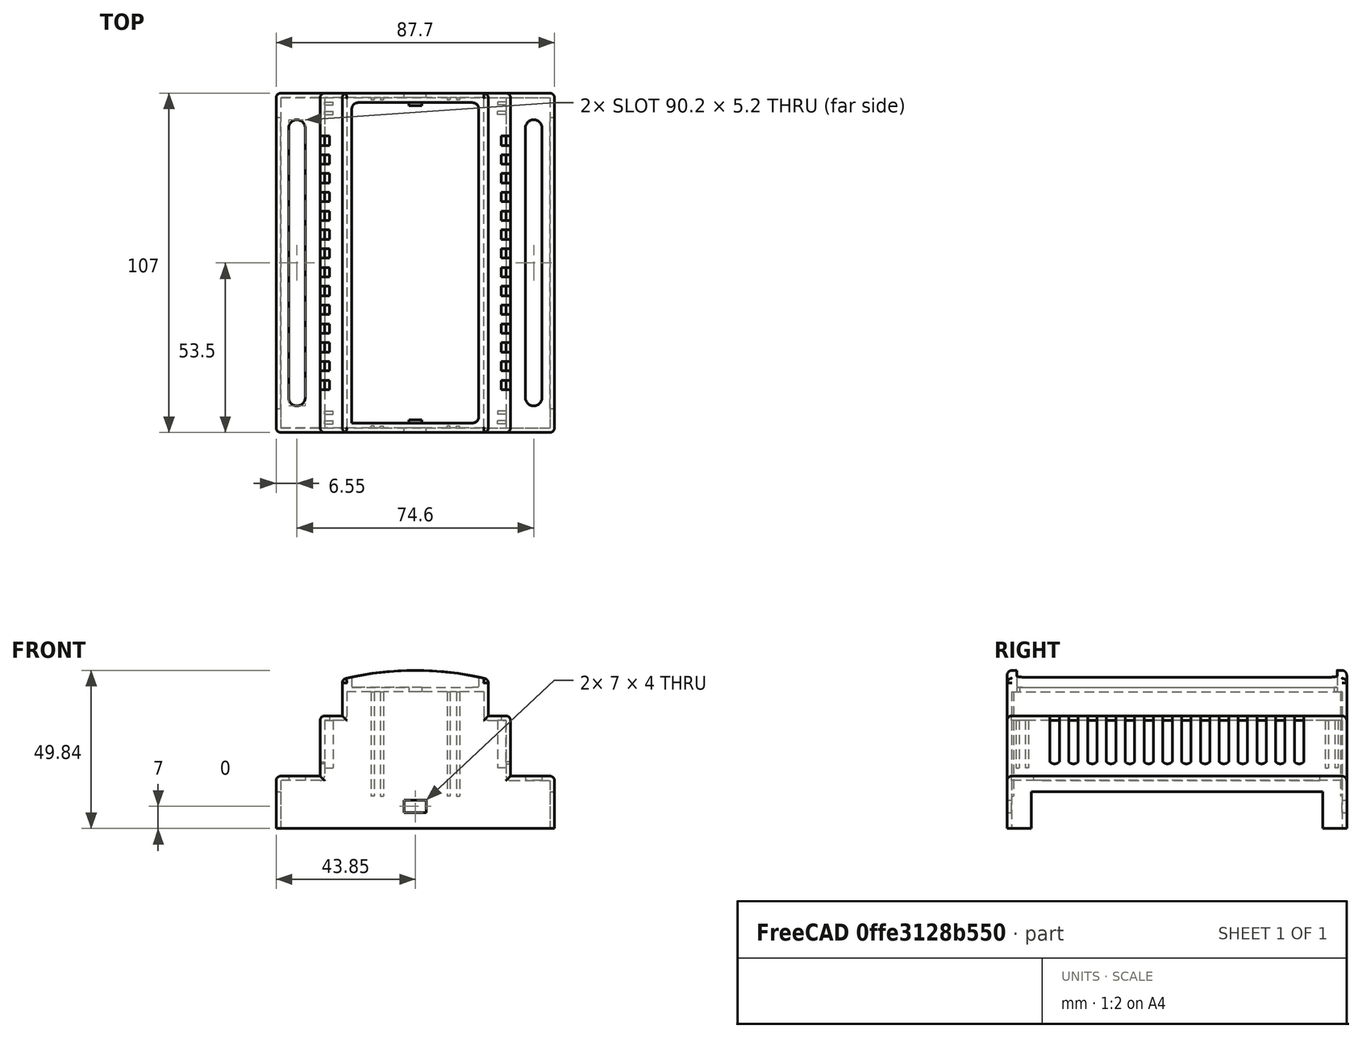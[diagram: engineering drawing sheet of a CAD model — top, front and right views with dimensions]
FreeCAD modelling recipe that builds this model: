
FCSTD DOCUMENT  (FreeCAD 1.0R39109 (Git))
Label: Parte de Arriba Vlad
License: All rights reserved
LicenseURL: https://en.wikipedia.org/wiki/All_rights_reserved
objects: Sketcher::SketchObject×15, PartDesign::Pad×9, PartDesign::Mirrored×7, PartDesign::Pocket×6, PartDesign::Fillet×4, PartDesign::Thickness×2, PartDesign::Plane×1, PartDesign::Body×1
note: 109 computed .brp shape members not serialized (recipe doc carries the construction recipe); baked Part::Feature solids carry a one-line shape summary decoded from their .brp

FEATURE [Sketcher::SketchObject] Sketch
  ArcFitTolerance = 1e-06
  AttachmentSupport = -> [XZ_Plane001]
  FullyConstrained = true
  MakeInternals = false
  MapMode = 5
  Placement = pos=(0,0,0) rot=(1,0,0;1.5708rad)
  sketch-geometry (12):
    g0: LineSegment StartX=-43.85 StartY=0 StartZ=0 EndX=43.85 EndY=0 EndZ=0
    g1: LineSegment StartX=-43.85 StartY=0 StartZ=0 EndX=-43.85 EndY=16.54 EndZ=0
    g2: LineSegment StartX=43.85 StartY=0 StartZ=0 EndX=43.85 EndY=16.54 EndZ=0
    g3: LineSegment StartX=-43.85 StartY=16.54 StartZ=0 EndX=-30 EndY=16.54 EndZ=0
    g4: LineSegment StartX=43.85 StartY=16.54 StartZ=0 EndX=30 EndY=16.54 EndZ=0
    g5: LineSegment StartX=-30 StartY=16.54 StartZ=0 EndX=-30 EndY=35.54 EndZ=0
    g6: LineSegment StartX=30 StartY=16.54 StartZ=0 EndX=30 EndY=35.54 EndZ=0
    g7: LineSegment StartX=-30 StartY=35.54 StartZ=0 EndX=-23 EndY=35.54 EndZ=0
    g8: LineSegment StartX=30 StartY=35.54 StartZ=0 EndX=23 EndY=35.54 EndZ=0
    g9: LineSegment StartX=23 StartY=35.54 StartZ=0 EndX=23 EndY=44.54 EndZ=0
    g10: LineSegment StartX=-23 StartY=35.54 StartZ=0 EndX=-23 EndY=44.54 EndZ=0
    g11: LineSegment StartX=-23 StartY=44.54 StartZ=0 EndX=23 EndY=44.54 EndZ=0
  constraints (36):
    c: Distance(g0) = 87.7
    c: PointOnObject(g0,g-1)
    c: PointOnObject(g0,g-1)
    c: Vertical(g1)
    c: Coincident(g1,g0)
    c: Vertical(g2)
    c: Coincident(g2,g0)
    c: Distance(g3) = 13.85
    c: Horizontal(g3)
    c: Coincident(g3,g1)
    c: Distance(g4) = 13.85
    c: Horizontal(g4)
    c: Coincident(g4,g2)
    c: Vertical(g5)
    c: Coincident(g5,g3)
    c: Vertical(g6)
    c: Coincident(g6,g4)
    c: Distance(g7) = 7
    c: Horizontal(g7)
    c: Coincident(g7,g5)
    c: Distance(g8) = 7
    c: Horizontal(g8)
    c: Coincident(g8,g6)
    c: Vertical(g9)
    c: Coincident(g9,g8)
    c: Vertical(g10)
    c: Coincident(g10,g7)
    c: Coincident(g11,g10)
    c: Coincident(g11,g9)
    c: Equal(g1,g2)
    c: Equal(g5,g6)
    c: Equal(g10,g9)
    c: Distance(g0,g11) = 44.54
    c: DistanceY(g1,g1) = 16.54
    c: Distance(g5,g0) = 35.54
    c: Distance(g10,g-2) = 23
FEATURE [PartDesign::Pad] Pad
  Direction = (0,-1,2e-16)
  Length = 107
  Length2 = 10
  Placement = pos=(0,0,0) rot=(1,0,0;1.5708rad)
  Profile = -> Sketch
  ReferenceAxis = -> Sketch [N_Axis]
  Refine = true
  Suppressed = false
  Type = 0
FEATURE [PartDesign::Thickness] Thickness
  Base = -> Pad
  BaseFeature = -> Pad
  Intersection = false
  Join = 0
  Mode = 0
  Placement = pos=(0,0,0) rot=(1,0,0;1.5708rad)
  Refine = true
  Reversed = true
  SupportTransform = false
  Suppressed = false
  Value = 1.4
FEATURE [PartDesign::Thickness] Thickness001
  Base = -> Thickness [Face1]
  BaseFeature = -> Thickness
  Intersection = false
  Join = 0
  Mode = 0
  Refine = true
  Reversed = true
  SupportTransform = false
  Suppressed = false
  Value = 1.4
FEATURE [Sketcher::SketchObject] Sketch001
  ArcFitTolerance = 1e-06
  AttachmentSupport = -> [Thickness001]
  FullyConstrained = true
  MakeInternals = false
  MapMode = 5
  Placement = pos=(-43.85,0,0) rot=(0.57735,-0.57735,-0.57735;2.0944rad)
  sketch-geometry (4):
    g0: LineSegment StartX=7.575 StartY=0 StartZ=0 EndX=99.425 EndY=0 EndZ=0
    g1: LineSegment StartX=99.425 StartY=0 StartZ=0 EndX=99.425 EndY=11.6 EndZ=0
    g2: LineSegment StartX=99.425 StartY=11.6 StartZ=0 EndX=7.575 EndY=11.6 EndZ=0
    g3: LineSegment StartX=7.575 StartY=11.6 StartZ=0 EndX=7.575 EndY=0 EndZ=0
  constraints (12):
    c: Coincident(g0,g1)
    c: Coincident(g1,g2)
    c: Coincident(g2,g3)
    c: Coincident(g3,g0)
    c: Horizontal(g0)
    c: Horizontal(g2)
    c: Vertical(g1)
    c: Vertical(g3)
    c: PointOnObject(g0,g-1)
    c: DistanceX(g2,g2) = 91.85
    c: DistanceY(g1,g1) = 11.6
    c: DistanceX(g-1,g0) = 7.575
FEATURE [PartDesign::Pocket] Pocket
  BaseFeature = -> Thickness001
  Direction = (1,0,0)
  Length = 5
  Length2 = 5
  Profile = -> Sketch001
  ReferenceAxis = -> Sketch001 [N_Axis]
  Refine = true
  Suppressed = false
  Type = 1
FEATURE [Sketcher::SketchObject] Sketch002
  ArcFitTolerance = 1e-06
  AttachmentSupport = -> [Pocket]
  FullyConstrained = true
  MakeInternals = false
  MapMode = 5
  Placement = pos=(0,4.2e-15,0) rot=(0,0.707107,0.707107;3.14159rad)
  sketch-geometry (4):
    g0: LineSegment StartX=-23 StartY=44.54 StartZ=0 EndX=23 EndY=44.54 EndZ=0
    g1: LineSegment StartX=-23 StartY=44.54 StartZ=0 EndX=-23 EndY=47.04 EndZ=0
    g2: LineSegment StartX=23 StartY=44.54 StartZ=0 EndX=23 EndY=47.04 EndZ=0
    g3: ArcOfCircle CenterX=1.7e-15 CenterY=-46.0243 CenterZ=0 NormalX=0 NormalY=0 NormalZ=1 AngleXU=0 Radius=95.8643 StartAngle=1.32851 EndAngle=1.81308
  constraints (13):
    c: Distance(g0) = 46
    c: Horizontal(g0)
    c: Distance(g-1,g0) = 44.54
    c: Distance(g0,g-2) = 23
    c: Distance(g1) = 2.5
    c: Coincident(g1,g0)
    c: Vertical(g1)
    c: Distance(g2) = 2.5
    c: Coincident(g2,g0)
    c: Vertical(g2)
    c: Coincident(g3,g1)
    c: Coincident(g3,g2)
    c: Distance(g3,g0) = -5.3
FEATURE [PartDesign::Pad] Pad001
  BaseFeature = -> Pocket
  Direction = (0,1,-2e-16)
  Length = 107
  Length2 = 10
  Profile = -> Sketch002
  ReferenceAxis = -> Sketch002 [N_Axis]
  Refine = true
  Suppressed = false
  Type = 0
FEATURE [Sketcher::SketchObject] Sketch003
  ArcFitTolerance = 1e-06
  AttachmentSupport = -> [Pad001]
  ExternalGeometry = -> [Pad001]
  FullyConstrained = true
  MakeInternals = false
  MapMode = 5
  Placement = pos=(0,4.2e-15,0) rot=(0,0.707107,0.707107;3.14159rad)
  sketch-geometry (4):
    g0: LineSegment StartX=-23 StartY=44.54 StartZ=0 EndX=-23 EndY=47.04 EndZ=0
    g1: LineSegment StartX=23 StartY=44.54 StartZ=0 EndX=23 EndY=47.04 EndZ=0
    g2: ArcOfCircle CenterX=4.82e-14 CenterY=-46.0243 CenterZ=0 NormalX=0 NormalY=0 NormalZ=1 AngleXU=0 Radius=95.8643 StartAngle=1.32851 EndAngle=1.81308
    g3: LineSegment StartX=-23 StartY=44.54 StartZ=0 EndX=23 EndY=44.54 EndZ=0
  constraints (9):
    c: Distance(g0) = 2.5
    c: Coincident(g2,g0)
    c: Coincident(g2,g1)
    c: Coincident(g3,g-3)
    c: Coincident(g3,g-3)
    c: Perpendicular(g0,g3) = 4.71239
    c: Distance(g2,g3) = -5.3
    c: Perpendicular(g1,g3) = 4.71239
    c: DistanceY(g1,g1) = 2.5
FEATURE [PartDesign::Pad] Pad002
  BaseFeature = -> Pad001
  Direction = (0,1,-2e-16)
  Length = 3
  Length2 = 10
  Profile = -> Sketch003
  ReferenceAxis = -> Sketch003 [N_Axis]
  Refine = true
  Reversed = true
  Suppressed = false
  Type = 0
FEATURE [Sketcher::SketchObject] Sketch004
  ArcFitTolerance = 1e-06
  AttachmentSupport = -> [Pad002]
  ExternalGeometry = -> [Pad002]
  FullyConstrained = true
  MakeInternals = false
  MapMode = 5
  Placement = pos=(0,-107,0) rot=(1,0,0;1.5708rad)
  sketch-geometry (4):
    g0: LineSegment StartX=-23 StartY=44.54 StartZ=0 EndX=23 EndY=44.54 EndZ=0
    g1: LineSegment StartX=23 StartY=44.54 StartZ=0 EndX=23 EndY=47.04 EndZ=0
    g2: LineSegment StartX=-23 StartY=44.54 StartZ=0 EndX=-23 EndY=47.04 EndZ=0
    g3: ArcOfCircle CenterX=3.7756e-12 CenterY=-46.0243 CenterZ=0 NormalX=0 NormalY=0 NormalZ=1 AngleXU=0 Radius=95.8643 StartAngle=1.32851 EndAngle=1.81308
  constraints (9):
    c: Coincident(g0,g-5)
    c: Coincident(g0,g-6)
    c: Coincident(g1,g0)
    c: Coincident(g1,g-6)
    c: Coincident(g2,g0)
    c: Coincident(g2,g-5)
    c: Coincident(g3,g2)
    c: Coincident(g3,g1)
    c: Tangent(g3,g-4)
FEATURE [PartDesign::Pad] Pad003
  BaseFeature = -> Pad002
  Direction = (0,-1,2e-16)
  Length = 3
  Length2 = 10
  Profile = -> Sketch004
  ReferenceAxis = -> Sketch004 [N_Axis]
  Refine = true
  Reversed = true
  Suppressed = false
  Type = 0
FEATURE [Sketcher::SketchObject] Sketch005
  ArcFitTolerance = 1e-06
  AttachmentSupport = -> [Pad003]
  ExternalGeometry = -> [Pad003]
  FullyConstrained = true
  MakeInternals = false
  MapMode = 5
  Placement = pos=(23,-8.5e-15,1.304e-13) rot=(0.57735,0.57735,0.57735;2.0944rad)
  sketch-geometry (4):
    g0: LineSegment StartX=-104 StartY=49.84 StartZ=0 EndX=-104 EndY=44.54 EndZ=0
    g1: LineSegment StartX=-104 StartY=44.54 StartZ=0 EndX=-3 EndY=44.54 EndZ=0
    g2: LineSegment StartX=-3 StartY=49.84 StartZ=0 EndX=-3 EndY=44.54 EndZ=0
    g3: LineSegment StartX=-104 StartY=49.84 StartZ=0 EndX=-3 EndY=49.84 EndZ=0
  constraints (8):
    c: Coincident(g0,g-5)
    c: Coincident(g0,g-3)
    c: Coincident(g1,g0)
    c: Coincident(g1,g-3)
    c: Coincident(g2,g-4)
    c: Coincident(g2,g1)
    c: Coincident(g3,g0)
    c: Coincident(g3,g2)
FEATURE [PartDesign::Pad] Pad004
  BaseFeature = -> Pad003
  Direction = (1,0,5.8e-15)
  Length = 3
  Length2 = 10
  Profile = -> Sketch005
  ReferenceAxis = -> Sketch005 [N_Axis]
  Refine = true
  Reversed = true
  Suppressed = false
  Type = 0
FEATURE [PartDesign::Mirrored] Mirrored
  BaseFeature = -> Pad004
  MirrorPlane = -> YZ_Plane001
  Originals = -> [Pad004]
  Refine = true
  Suppressed = false
  TransformMode = 0
FEATURE [Sketcher::SketchObject] Sketch006
  ArcFitTolerance = 1e-06
  AttachmentSupport = -> [Mirrored]
  FullyConstrained = true
  MakeInternals = false
  MapMode = 5
  Placement = pos=(0,7.3e-15,16.54) rot=(0,0,1;0rad)
  sketch-geometry (4):
    g0: ArcOfCircle CenterX=37.3 CenterY=-11 CenterZ=0 NormalX=0 NormalY=0 NormalZ=1 AngleXU=0 Radius=2.6 StartAngle=2.2037e-12 EndAngle=3.14159
    g1: ArcOfCircle CenterX=37.3 CenterY=-96 CenterZ=0 NormalX=0 NormalY=0 NormalZ=1 AngleXU=0 Radius=2.6 StartAngle=3.14159 EndAngle=6.28319
    g2: LineSegment StartX=39.9 StartY=-11 StartZ=0 EndX=39.9 EndY=-96 EndZ=0
    g3: LineSegment StartX=34.7 StartY=-11 StartZ=0 EndX=34.7 EndY=-96 EndZ=0
  constraints (10):
    c: Tangent(g0,g2) = 1.5708
    c: Tangent(g0,g3) = -1.5708
    c: Tangent(g1,g2) = 1.5708
    c: Tangent(g1,g3) = -1.5708
    c: Equal(g0,g1)
    c: Vertical(g2)
    c: Distance(g2,g3) = 5.2
    c: DistanceY(g2,g2) = 85
    c: Distance(g0,g-2) = 37.3
    c: Distance(g0,g-1) = 11
FEATURE [PartDesign::Pocket] Pocket001
  BaseFeature = -> Mirrored
  Direction = (0,0,-1)
  Length = 5
  Length2 = 5
  Profile = -> Sketch006
  ReferenceAxis = -> Sketch006 [N_Axis]
  Refine = true
  Suppressed = false
  Type = 0
FEATURE [PartDesign::Mirrored] Mirrored001
  BaseFeature = -> Pocket001
  MirrorPlane = -> YZ_Plane001
  Originals = -> [Pocket001]
  Refine = true
  Suppressed = false
  TransformMode = 0
FEATURE [Sketcher::SketchObject] Sketch007
  ArcFitTolerance = 1e-06
  AttachmentSupport = -> [Mirrored001]
  ExternalGeometry = -> [Mirrored001]
  FullyConstrained = true
  MakeInternals = false
  MapMode = 5
  Placement = pos=(30,0,0) rot=(0.57735,0.57735,0.57735;2.0944rad)
  sketch-geometry (57):
    g0: LineSegment [constr] StartX=-53.5 StartY=35.54 StartZ=0 EndX=-53.5 EndY=16.54 EndZ=0
    g1: LineSegment StartX=-16.4625 StartY=35.54 StartZ=0 EndX=-13.4995 EndY=35.54 EndZ=0
    g2: LineSegment StartX=-13.4995 StartY=35.54 StartZ=0 EndX=-13.4995 EndY=21.04 EndZ=0
    g3: LineSegment StartX=-16.4625 StartY=35.54 StartZ=0 EndX=-16.4625 EndY=21.04 EndZ=0
    g4: ArcOfCircle CenterX=-14.981 CenterY=22.3836 CenterZ=0 NormalX=0 NormalY=0 NormalZ=1 AngleXU=0 Radius=2 StartAngle=3.8782 EndAngle=5.54658
    g5: LineSegment StartX=-22.3885 StartY=35.54 StartZ=0 EndX=-19.4255 EndY=35.54 EndZ=0
    g6: LineSegment StartX=-19.4255 StartY=35.54 StartZ=0 EndX=-19.4255 EndY=21.04 EndZ=0
    g7: LineSegment StartX=-22.3885 StartY=35.54 StartZ=0 EndX=-22.3885 EndY=21.04 EndZ=0
    g8: ArcOfCircle CenterX=-20.907 CenterY=22.3836 CenterZ=0 NormalX=0 NormalY=0 NormalZ=1 AngleXU=0 Radius=2 StartAngle=3.8782 EndAngle=5.54658
    g9: LineSegment StartX=-28.3145 StartY=35.54 StartZ=0 EndX=-25.3515 EndY=35.54 EndZ=0
    g10: LineSegment StartX=-25.3515 StartY=35.54 StartZ=0 EndX=-25.3515 EndY=21.04 EndZ=0
    g11: LineSegment StartX=-28.3145 StartY=35.54 StartZ=0 EndX=-28.3145 EndY=21.04 EndZ=0
    g12: ArcOfCircle CenterX=-26.833 CenterY=22.3836 CenterZ=0 NormalX=0 NormalY=0 NormalZ=1 AngleXU=0 Radius=2 StartAngle=3.8782 EndAngle=5.54658
    g13: LineSegment StartX=-34.2405 StartY=35.54 StartZ=0 EndX=-31.2775 EndY=35.54 EndZ=0
    g14: LineSegment StartX=-34.2405 StartY=35.54 StartZ=0 EndX=-34.2405 EndY=21.04 EndZ=0
    g15: LineSegment StartX=-31.2775 StartY=35.54 StartZ=0 EndX=-31.2775 EndY=21.04 EndZ=0
    g16: ArcOfCircle CenterX=-32.759 CenterY=22.3836 CenterZ=0 NormalX=0 NormalY=0 NormalZ=1 AngleXU=0 Radius=2 StartAngle=3.8782 EndAngle=5.54658
    g17: LineSegment StartX=-40.1665 StartY=35.54 StartZ=0 EndX=-37.2035 EndY=35.54 EndZ=0
    g18: LineSegment StartX=-37.2035 StartY=35.54 StartZ=0 EndX=-37.2035 EndY=21.04 EndZ=0
    g19: LineSegment StartX=-40.1665 StartY=35.54 StartZ=0 EndX=-40.1665 EndY=21.04 EndZ=0
    g20: ArcOfCircle CenterX=-38.685 CenterY=22.3836 CenterZ=0 NormalX=0 NormalY=0 NormalZ=1 AngleXU=0 Radius=2 StartAngle=3.8782 EndAngle=5.54658
    g21: LineSegment StartX=-46.0925 StartY=35.54 StartZ=0 EndX=-43.1295 EndY=35.54 EndZ=0
    g22: LineSegment StartX=-43.1295 StartY=35.54 StartZ=0 EndX=-43.1295 EndY=21.04 EndZ=0
    g23: LineSegment StartX=-46.0925 StartY=35.54 StartZ=0 EndX=-46.0925 EndY=21.04 EndZ=0
    g24: ArcOfCircle CenterX=-44.611 CenterY=22.3836 CenterZ=0 NormalX=0 NormalY=0 NormalZ=1 AngleXU=0 Radius=2 StartAngle=3.8782 EndAngle=5.54658
    g25: LineSegment StartX=-52.0185 StartY=35.54 StartZ=0 EndX=-49.0555 EndY=35.54 EndZ=0
    g26: LineSegment StartX=-49.0555 StartY=35.54 StartZ=0 EndX=-49.0555 EndY=21.04 EndZ=0
    g27: LineSegment StartX=-52.0185 StartY=35.54 StartZ=0 EndX=-52.0185 EndY=21.04 EndZ=0
    g28: ArcOfCircle CenterX=-50.537 CenterY=22.3836 CenterZ=0 NormalX=0 NormalY=0 NormalZ=1 AngleXU=0 Radius=2 StartAngle=3.8782 EndAngle=5.54658
    g29: LineSegment StartX=-57.9445 StartY=35.54 StartZ=0 EndX=-54.9815 EndY=35.54 EndZ=0
    g30: LineSegment StartX=-54.9815 StartY=35.54 StartZ=0 EndX=-54.9815 EndY=21.04 EndZ=0
    g31: LineSegment StartX=-57.9445 StartY=35.54 StartZ=0 EndX=-57.9445 EndY=21.04 EndZ=0
    g32: ArcOfCircle CenterX=-56.463 CenterY=22.3836 CenterZ=0 NormalX=0 NormalY=0 NormalZ=1 AngleXU=0 Radius=2 StartAngle=3.8782 EndAngle=5.54658
    g33: LineSegment StartX=-63.8705 StartY=35.54 StartZ=0 EndX=-60.9075 EndY=35.54 EndZ=0
    g34: LineSegment StartX=-60.9075 StartY=35.54 StartZ=0 EndX=-60.9075 EndY=21.04 EndZ=0
    g35: LineSegment StartX=-63.8705 StartY=35.54 StartZ=0 EndX=-63.8705 EndY=21.04 EndZ=0
    g36: ArcOfCircle CenterX=-62.389 CenterY=22.3836 CenterZ=0 NormalX=0 NormalY=0 NormalZ=1 AngleXU=0 Radius=2 StartAngle=3.8782 EndAngle=5.54658
    g37: LineSegment StartX=-69.7965 StartY=35.54 StartZ=0 EndX=-66.8335 EndY=35.54 EndZ=0
    g38: LineSegment StartX=-66.8335 StartY=35.54 StartZ=0 EndX=-66.8335 EndY=21.04 EndZ=0
    g39: LineSegment StartX=-69.7965 StartY=35.54 StartZ=0 EndX=-69.7965 EndY=21.04 EndZ=0
    g40: ArcOfCircle CenterX=-68.315 CenterY=22.3836 CenterZ=0 NormalX=0 NormalY=0 NormalZ=1 AngleXU=0 Radius=2 StartAngle=3.8782 EndAngle=5.54658
    g41: LineSegment StartX=-75.7225 StartY=35.54 StartZ=0 EndX=-72.7595 EndY=35.54 EndZ=0
    g42: LineSegment StartX=-72.7595 StartY=35.54 StartZ=0 EndX=-72.7595 EndY=21.04 EndZ=0
    g43: LineSegment StartX=-75.7225 StartY=35.54 StartZ=0 EndX=-75.7225 EndY=21.04 EndZ=0
    g44: ArcOfCircle CenterX=-74.241 CenterY=22.3836 CenterZ=0 NormalX=0 NormalY=0 NormalZ=1 AngleXU=0 Radius=2 StartAngle=3.8782 EndAngle=5.54658
    g45: LineSegment StartX=-81.6485 StartY=35.54 StartZ=0 EndX=-78.6855 EndY=35.54 EndZ=0
    g46: LineSegment StartX=-78.6855 StartY=35.54 StartZ=0 EndX=-78.6855 EndY=21.04 EndZ=0
    g47: LineSegment StartX=-81.6485 StartY=35.54 StartZ=0 EndX=-81.6485 EndY=21.04 EndZ=0
    g48: ArcOfCircle CenterX=-80.167 CenterY=22.3836 CenterZ=0 NormalX=0 NormalY=0 NormalZ=1 AngleXU=0 Radius=2 StartAngle=3.8782 EndAngle=5.54658
    g49: LineSegment StartX=-87.5745 StartY=35.54 StartZ=0 EndX=-84.6115 EndY=35.54 EndZ=0
    g50: LineSegment StartX=-84.6115 StartY=35.54 StartZ=0 EndX=-84.6115 EndY=21.04 EndZ=0
    g51: LineSegment StartX=-87.5745 StartY=35.54 StartZ=0 EndX=-87.5745 EndY=21.04 EndZ=0
    g52: ArcOfCircle CenterX=-86.093 CenterY=22.3836 CenterZ=0 NormalX=0 NormalY=0 NormalZ=1 AngleXU=0 Radius=2 StartAngle=3.8782 EndAngle=5.54658
    g53: LineSegment StartX=-93.5005 StartY=35.54 StartZ=0 EndX=-90.5375 EndY=35.54 EndZ=0
    g54: LineSegment StartX=-90.5375 StartY=35.54 StartZ=0 EndX=-90.5375 EndY=21.04 EndZ=0
    g55: LineSegment StartX=-93.5005 StartY=35.54 StartZ=0 EndX=-93.5005 EndY=21.04 EndZ=0
    g56: ArcOfCircle CenterX=-92.019 CenterY=22.3836 CenterZ=0 NormalX=0 NormalY=0 NormalZ=1 AngleXU=0 Radius=2 StartAngle=3.8782 EndAngle=5.54658
  constraints (184):
    c: Symmetric(g-4,g-4,g0)
    c: Symmetric(g-3,g-3,g0)
    c: PointOnObject(g1,g-4)
    c: PointOnObject(g1,g-4)
    c: Distance(g2) = 14.5
    c: Vertical(g2)
    c: Coincident(g2,g1)
    c: Vertical(g3)
    c: Coincident(g3,g1)
    c: Coincident(g4,g3)
    c: Coincident(g4,g2)
    c: DistanceX(g1,g1) = 2.963
    c: Radius(g4) = 2
    c: Distance(g5) = 2.963
    c: Horizontal(g5)
    c: PointOnObject(g5,g-4)
    c: Vertical(g6)
    c: Coincident(g6,g5)
    c: Vertical(g7)
    c: Coincident(g7,g5)
    c: Equal(g2,g3)
    c: Equal(g3,g6)
    c: Equal(g6,g7)
    c: Distance(g3,g6) = 2.963
    c: Coincident(g8,g7)
    c: Coincident(g8,g6)
    c: Equal(g4,g8)
    c: Horizontal(g9)
    c: PointOnObject(g9,g-4)
    c: Vertical(g10)
    c: Coincident(g10,g9)
    c: Vertical(g11)
    c: Coincident(g11,g9)
    c: Coincident(g12,g11)
    c: Coincident(g12,g10)
    c: Equal(g5,g9)
    c: Equal(g6,g10)
    c: Equal(g10,g11)
    c: Equal(g4,g12)
    c: Distance(g7,g10) = 2.963
    c: PointOnObject(g13,g-4)
    c: PointOnObject(g13,g-4)
    c: Vertical(g14)
    c: Coincident(g14,g13)
    c: Vertical(g15)
    c: Coincident(g15,g13)
    c: Coincident(g16,g14)
    c: Coincident(g16,g15)
    c: Equal(g15,g14)
    c: Equal(g14,g2)
    c: Equal(g1,g13)
    c: Distance(g11,g15) = 2.963
    c: Equal(g4,g16)
    c: PointOnObject(g17,g-4)
    c: PointOnObject(g17,g-4)
    c: Vertical(g18)
    c: Coincident(g18,g17)
    c: Vertical(g19)
    c: Coincident(g19,g17)
    c: Coincident(g20,g19)
    c: Coincident(g20,g18)
    c: Distance(g14,g18) = 2.963
    c: Equal(g2,g18)
    c: Equal(g18,g19)
    c: Equal(g1,g17)
    c: Equal(g4,g20)
    c: PointOnObject(g21,g-4)
    c: PointOnObject(g21,g-4)
    c: Vertical(g22)
    c: Coincident(g22,g21)
    c: Vertical(g23)
    c: Coincident(g23,g21)
    c: Coincident(g24,g23)
    c: Coincident(g24,g22)
    c: Equal(g1,g21)
    c: Equal(g22,g23)
    c: Equal(g23,g2)
    c: Distance(g19,g22) = 2.963
    c: Equal(g4,g24)
    c: PointOnObject(g25,g-4)
    c: PointOnObject(g25,g-4)
    c: Vertical(g26)
    c: Coincident(g26,g25)
    c: Vertical(g27)
    c: Coincident(g27,g25)
    c: Coincident(g28,g27)
    c: Coincident(g28,g26)
    c: Equal(g2,g26)
    c: Equal(g26,g27)
    c: Equal(g1,g25)
    c: Equal(g4,g28)
    c: Distance(g23,g26) = 2.963
    c: PointOnObject(g29,g-4)
    c: PointOnObject(g29,g-4)
    c: Coincident(g30,g29)
    c: Vertical(g30)
    c: Coincident(g31,g29)
    c: Vertical(g31)
    c: Equal(g30,g31)
    c: Equal(g31,g3)
    c: Coincident(g32,g31)
    c: Coincident(g32,g30)
    c: Equal(g4,g32)
    c: Equal(g29,g1)
    c: Distance(g27,g30) = 2.963
    c: PointOnObject(g33,g-4)
    c: PointOnObject(g33,g-4)
    c: Coincident(g34,g33)
    c: Vertical(g34)
    c: Coincident(g35,g33)
    c: Vertical(g35)
    c: Equal(g35,g34)
    c: Equal(g34,g31)
    c: Equal(g33,g29)
    c: Coincident(g36,g35)
    c: Coincident(g36,g34)
    c: Equal(g32,g36)
    c: Distance(g31,g34) = 2.963
    c: PointOnObject(g37,g-4)
    c: PointOnObject(g37,g-4)
    c: Coincident(g38,g37)
    c: Vertical(g38)
    c: Coincident(g39,g37)
    c: Vertical(g39)
    c: Coincident(g40,g39)
    c: Coincident(g40,g38)
    c: Equal(g38,g39)
    c: Equal(g39,g35)
    c: Equal(g40,g36)
    c: Equal(g33,g37)
    c: Distance(g35,g38) = 2.963
    c: PointOnObject(g41,g-4)
    c: PointOnObject(g41,g-4)
    c: Coincident(g42,g41)
    c: Vertical(g42)
    c: Coincident(g43,g41)
    c: Vertical(g43)
    c: Coincident(g44,g43)
    c: Coincident(g44,g42)
    c: Equal(g43,g42)
    c: Equal(g42,g39)
    c: Equal(g41,g37)
    c: Equal(g44,g40)
    c: Distance(g39,g42) = 2.963
    c: PointOnObject(g45,g-4)
    c: PointOnObject(g45,g-4)
    c: Coincident(g46,g45)
    c: Vertical(g46)
    c: Coincident(g47,g45)
    c: Vertical(g47)
    c: Coincident(g48,g47)
    c: Coincident(g48,g46)
    c: Equal(g47,g46)
    c: Equal(g46,g43)
    c: Equal(g45,g41)
    c: Equal(g44,g48)
    c: Distance(g43,g46) = 2.963
    c: PointOnObject(g49,g-4)
    c: PointOnObject(g49,g-4)
    c: Coincident(g50,g49)
    c: Vertical(g50)
    c: Coincident(g51,g49)
    c: Vertical(g51)
    c: Coincident(g52,g51)
    c: Coincident(g52,g50)
    c: Equal(g51,g50)
    c: Equal(g50,g47)
    c: Equal(g49,g45)
    c: Equal(g48,g52)
    c: Distance(g47,g50) = 2.963
    c: PointOnObject(g53,g-4)
    c: PointOnObject(g53,g-4)
    c: Coincident(g54,g53)
    c: Vertical(g54)
    c: Coincident(g55,g53)
    c: Vertical(g55)
    c: Coincident(g56,g55)
    c: Coincident(g56,g54)
    c: Equal(g55,g54)
    c: Equal(g54,g51)
    c: Equal(g56,g52)
    c: Equal(g53,g49)
    c: Distance(g51,g54) = 2.963
    c: Distance(g0,g27) = 1.4815
FEATURE [PartDesign::Pocket] Pocket002
  BaseFeature = -> Mirrored001
  Direction = (-1,0,0)
  Length = 2.963
  Length2 = 5
  Profile = -> Sketch007
  ReferenceAxis = -> Sketch007 [N_Axis]
  Refine = true
  Suppressed = false
  Type = 0
FEATURE [PartDesign::Mirrored] Mirrored002
  BaseFeature = -> Pocket002
  MirrorPlane = -> YZ_Plane001
  Originals = -> [Pocket002]
  Refine = true
  Suppressed = false
  TransformMode = 0
FEATURE [PartDesign::Fillet] Fillet
  Base = -> Mirrored002 [Edge272,Edge110,Edge99,Edge166,Edge114,Edge118,Edge122,Edge126,Edge130,Edge134,Edge138,Edge142,Edge146,Edge150,Edge154,Edge158,Edge162,Edge20,Edge98,Edge97,Edge96]
  BaseFeature = -> Mirrored002
  Radius = 1.5
  Refine = true
  SupportTransform = false
  Suppressed = false
  UseAllEdges = false
FEATURE [PartDesign::Mirrored] Mirrored003
  BaseFeature = -> Fillet
  MirrorPlane = -> YZ_Plane001
  Originals = -> [Fillet]
  Refine = true
  Suppressed = false
  TransformMode = 0
FEATURE [Sketcher::SketchObject] Sketch008
  ArcFitTolerance = 1e-06
  AttachmentSupport = -> [Mirrored003]
  FullyConstrained = true
  MakeInternals = false
  MapMode = 5
  Placement = pos=(0,-107,3.53e-14) rot=(1,0,0;1.5708rad)
  sketch-geometry (4):
    g0: LineSegment StartX=-3.5 StartY=9 StartZ=0 EndX=3.5 EndY=9 EndZ=0
    g1: LineSegment StartX=-3.5 StartY=9 StartZ=0 EndX=-3.5 EndY=5 EndZ=0
    g2: LineSegment StartX=3.5 StartY=9 StartZ=0 EndX=3.5 EndY=5 EndZ=0
    g3: LineSegment StartX=-3.5 StartY=5 StartZ=0 EndX=3.5 EndY=5 EndZ=0
  constraints (12):
    c: Distance(g0) = 7
    c: Horizontal(g0)
    c: Vertical(g1)
    c: Coincident(g1,g0)
    c: Distance(g2) = 4
    c: Vertical(g2)
    c: Coincident(g2,g0)
    c: Coincident(g3,g1)
    c: Coincident(g3,g2)
    c: Distance(g-2,g1) = 3.5
    c: Equal(g2,g1)
    c: Distance(g-1,g3) = 5
FEATURE [PartDesign::Pocket] Pocket003
  BaseFeature = -> Mirrored003
  Direction = (0,1,-2e-16)
  Length = 5
  Length2 = 5
  Profile = -> Sketch008
  ReferenceAxis = -> Sketch008 [N_Axis]
  Refine = true
  Suppressed = false
  Type = 1
FEATURE [Sketcher::SketchObject] Sketch009
  ArcFitTolerance = 1e-06
  AttachmentSupport = -> [Pocket003]
  ExternalGeometry = -> [Pocket003]
  FullyConstrained = true
  MakeInternals = false
  MapMode = 5
  Placement = pos=(0,-104,0) rot=(1,0,0;1.5708rad)
  sketch-geometry (8):
    g0: LineSegment StartX=-23 StartY=47.04 StartZ=0 EndX=-23 EndY=49.84 EndZ=0
    g1: LineSegment StartX=-23 StartY=49.84 StartZ=0 EndX=-20 EndY=49.84 EndZ=0
    g2: LineSegment StartX=-20 StartY=49.84 StartZ=0 EndX=-20 EndY=47.7305 EndZ=0
    g3: ArcOfCircle CenterX=9.71783e-05 CenterY=-46.0247 CenterZ=0 NormalX=0 NormalY=0 NormalZ=1 AngleXU=0 Radius=95.8647 StartAngle=1.78097 EndAngle=1.81308
    g4: LineSegment StartX=20 StartY=49.84 StartZ=0 EndX=23 EndY=49.84 EndZ=0
    g5: LineSegment StartX=23 StartY=49.84 StartZ=0 EndX=23 EndY=47.04 EndZ=0
    g6: LineSegment StartX=20 StartY=49.84 StartZ=0 EndX=20 EndY=47.7305 EndZ=0
    g7: ArcOfCircle CenterX=-7.58465e-05 CenterY=-46.0246 CenterZ=0 NormalX=0 NormalY=0 NormalZ=1 AngleXU=0 Radius=95.8646 StartAngle=1.32851 EndAngle=1.36062
  constraints (19):
    c: Coincident(g0,g-6)
    c: Coincident(g0,g-6)
    c: Coincident(g1,g0)
    c: Coincident(g1,g-5)
    c: Coincident(g2,g1)
    c: Coincident(g2,g-4)
    c: Coincident(g3,g0)
    c: Coincident(g3,g2)
    c: Tangent(g3,g-3)
    c: Coincident(g4,g-8)
    c: Coincident(g4,g-9)
    c: Coincident(g5,g4)
    c: PointOnObject(g5,g-10)
    c: Vertical(g5)
    c: Coincident(g6,g4)
    c: Coincident(g6,g-10)
    c: Coincident(g7,g6)
    c: Coincident(g7,g5)
    c: Tangent(g7,g-10)
FEATURE [PartDesign::Pocket] Pocket004
  BaseFeature = -> Pocket003
  Direction = (0,1,-2e-16)
  Length = 0
  Length2 = 5
  Profile = -> Sketch009
  ReferenceAxis = -> Sketch009 [N_Axis]
  Refine = true
  Suppressed = false
  Type = 3
  UpToFace = -> Pocket003 [Face89]
FEATURE [PartDesign::Mirrored] Mirrored004
  BaseFeature = -> Pocket004
  MirrorPlane = -> YZ_Plane001
  Originals = -> [Fillet]
  Refine = true
  Suppressed = false
  TransformMode = 0
FEATURE [PartDesign::Fillet] Fillet001
  Base = -> Mirrored004 [Edge26,Edge28,Edge32,Edge34,Edge33,Edge5,Edge22,Edge24,Edge25,Edge29]
  BaseFeature = -> Mirrored004
  Radius = 1.5
  Refine = true
  SupportTransform = false
  Suppressed = false
  UseAllEdges = false
FEATURE [Sketcher::SketchObject] Sketch010
  ArcFitTolerance = 1e-06
  FullyConstrained = true
  MakeInternals = false
  MapMode = 5
  Placement = pos=(0,1.96e-14,44.54) rot=(0,0,1;0rad)
  sketch-geometry (8):
    g0: LineSegment StartX=-2 StartY=-3 StartZ=0 EndX=2 EndY=-3 EndZ=0
    g1: LineSegment StartX=-2 StartY=-3 StartZ=0 EndX=-2 EndY=-4 EndZ=0
    g2: LineSegment StartX=2 StartY=-3 StartZ=0 EndX=2 EndY=-4 EndZ=0
    g3: LineSegment StartX=-2 StartY=-4 StartZ=0 EndX=2 EndY=-4 EndZ=0
    g4: LineSegment StartX=2 StartY=-104 StartZ=0 EndX=-2 EndY=-104 EndZ=0
    g5: LineSegment StartX=2 StartY=-104 StartZ=0 EndX=2 EndY=-103 EndZ=0
    g6: LineSegment StartX=-2 StartY=-104 StartZ=0 EndX=-2 EndY=-103 EndZ=0
    g7: LineSegment StartX=2 StartY=-103 StartZ=0 EndX=-2 EndY=-103 EndZ=0
  constraints (24):
    c: PointOnObject(g0,g-3)
    c: PointOnObject(g0,g-3)
    c: Distance(g1) = 1
    c: Vertical(g1)
    c: Coincident(g1,g0)
    c: Distance(g2) = 1
    c: Vertical(g2)
    c: Coincident(g2,g0)
    c: Coincident(g3,g1)
    c: Coincident(g3,g2)
    c: Distance(g-2,g1) = 2
    c: Distance(g0,g0) = 4
    c: PointOnObject(g4,g-4)
    c: PointOnObject(g4,g-4)
    c: Distance(g5) = 1
    c: Vertical(g5)
    c: Coincident(g5,g4)
    c: Distance(g6) = 1
    c: Vertical(g6)
    c: Coincident(g6,g4)
    c: Coincident(g7,g5)
    c: Coincident(g7,g6)
    c: Distance(g-2,g5) = 2
    c: DistanceX(g4,g4) = 4
FEATURE [PartDesign::Pocket] Pocket005
  BaseFeature = -> Fillet001
  Direction = (0,0,-1)
  Length = 5
  Length2 = 5
  Profile = -> Sketch010
  ReferenceAxis = -> Sketch010 [N_Axis]
  Refine = true
  Suppressed = false
  Type = 0
FEATURE [PartDesign::Fillet] Fillet002
  Base = -> Pocket005 [Edge3,Edge78,Edge86,Edge10]
  BaseFeature = -> Pocket005
  Radius = 1.5
  Refine = true
  SupportTransform = false
  Suppressed = false
  UseAllEdges = false
FEATURE [Sketcher::SketchObject] Sketch011
  ArcFitTolerance = 1e-06
  FullyConstrained = true
  MakeInternals = false
  MapMode = 5
  Placement = pos=(0,-105.6,0) rot=(0,0.707107,0.707107;3.14159rad)
  sketch-geometry (9):
    g0: LineSegment [constr] StartX=-12 StartY=43.14 StartZ=0 EndX=-12 EndY=10.2 EndZ=0
    g1: LineSegment StartX=-11 StartY=43.14 StartZ=0 EndX=-11 EndY=10.2 EndZ=0
    g2: LineSegment StartX=-10 StartY=43.14 StartZ=0 EndX=-10 EndY=10.2 EndZ=0
    g3: LineSegment StartX=-11 StartY=10.2 StartZ=0 EndX=-10 EndY=10.2 EndZ=0
    g4: LineSegment StartX=-11 StartY=43.14 StartZ=0 EndX=-10 EndY=43.14 EndZ=0
    g5: LineSegment StartX=-13 StartY=43.14 StartZ=0 EndX=-13 EndY=10.2 EndZ=0
    g6: LineSegment StartX=-14 StartY=43.14 StartZ=0 EndX=-14 EndY=10.2 EndZ=0
    g7: LineSegment StartX=-13 StartY=10.2 StartZ=0 EndX=-14 EndY=10.2 EndZ=0
    g8: LineSegment StartX=-13 StartY=43.14 StartZ=0 EndX=-14 EndY=43.14 EndZ=0
  constraints (25):
    c: Distance(g0) = 32.94
    c: Vertical(g0)
    c: PointOnObject(g0,g-3)
    c: Distance(g-2,g0) = 12
    c: PointOnObject(g1,g-3)
    c: Vertical(g1)
    c: PointOnObject(g2,g-3)
    c: Vertical(g2)
    c: Equal(g2,g0)
    c: Distance(g3) = 1
    c: Coincident(g3,g1)
    c: Perpendicular(g2,g3) = 1.5708
    c: Coincident(g4,g1)
    c: Coincident(g4,g2)
    c: Distance(g1,g0) = 1
    c: Vertical(g5)
    c: Vertical(g6)
    c: Distance(g7) = 1
    c: Coincident(g7,g5)
    c: Perpendicular(g6,g7) = 4.71239
    c: Coincident(g8,g5)
    c: Coincident(g8,g6)
    c: Symmetric(g1,g5,g0)
    c: Equal(g0,g1)
    c: Equal(g6,g0)
FEATURE [PartDesign::Pad] Pad005
  BaseFeature = -> Fillet002
  Direction = (0,1,-2e-16)
  Length = 0.63
  Length2 = 10
  Profile = -> Sketch011
  ReferenceAxis = -> Sketch011 [N_Axis]
  Refine = true
  Suppressed = false
  Type = 0
FEATURE [PartDesign::Mirrored] Mirrored005
  BaseFeature = -> Pad005
  MirrorPlane = -> YZ_Plane001
  Originals = -> [Pad005]
  Refine = true
  Suppressed = false
  TransformMode = 0
FEATURE [Sketcher::SketchObject] Sketch012
  ArcFitTolerance = 1e-06
  AttachmentSupport = -> [Mirrored005]
  ExternalGeometry = -> [Mirrored005]
  FullyConstrained = true
  MakeInternals = false
  MapMode = 5
  Placement = pos=(0,-1.4,0) rot=(1,0,0;1.5708rad)
  sketch-geometry (16):
    g0: LineSegment StartX=-14 StartY=43.14 StartZ=0 EndX=-13 EndY=43.14 EndZ=0
    g1: LineSegment StartX=-11 StartY=43.14 StartZ=0 EndX=-10 EndY=43.14 EndZ=0
    g2: LineSegment StartX=-14 StartY=43.14 StartZ=0 EndX=-14 EndY=10.2 EndZ=0
    g3: LineSegment StartX=-14 StartY=10.2 StartZ=0 EndX=-13 EndY=10.2 EndZ=0
    g4: LineSegment StartX=-13 StartY=10.2 StartZ=0 EndX=-13 EndY=43.14 EndZ=0
    g5: LineSegment StartX=-11 StartY=43.14 StartZ=0 EndX=-11 EndY=10.2 EndZ=0
    g6: LineSegment StartX=-11 StartY=10.2 StartZ=0 EndX=-10 EndY=10.2 EndZ=0
    g7: LineSegment StartX=-10 StartY=10.2 StartZ=0 EndX=-10 EndY=43.14 EndZ=0
    g8: LineSegment StartX=10 StartY=43.14 StartZ=0 EndX=11 EndY=43.14 EndZ=0
    g9: LineSegment StartX=10 StartY=43.14 StartZ=0 EndX=10 EndY=10.2 EndZ=0
    g10: LineSegment StartX=10 StartY=10.2 StartZ=0 EndX=11 EndY=10.2 EndZ=0
    g11: LineSegment StartX=11 StartY=10.2 StartZ=0 EndX=11 EndY=43.14 EndZ=0
    g12: LineSegment StartX=13 StartY=43.14 StartZ=0 EndX=14 EndY=43.14 EndZ=0
    g13: LineSegment StartX=13 StartY=43.14 StartZ=0 EndX=13 EndY=10.2 EndZ=0
    g14: LineSegment StartX=13 StartY=10.2 StartZ=0 EndX=14 EndY=10.2 EndZ=0
    g15: LineSegment StartX=14 StartY=10.2 StartZ=0 EndX=14 EndY=43.14 EndZ=0
  constraints (32):
    c: Coincident(g0,g-16)
    c: Coincident(g0,g-15)
    c: Coincident(g1,g-13)
    c: Coincident(g1,g-14)
    c: Coincident(g2,g0)
    c: Coincident(g2,g-18)
    c: Coincident(g3,g2)
    c: Coincident(g3,g-18)
    c: Coincident(g4,g3)
    c: Coincident(g4,g0)
    c: Coincident(g5,g1)
    c: Coincident(g5,g-17)
    c: Coincident(g6,g5)
    c: Coincident(g6,g-17)
    c: Coincident(g7,g6)
    c: Coincident(g7,g1)
    c: Coincident(g8,g-7)
    c: Coincident(g8,g-8)
    c: Coincident(g9,g8)
    c: Coincident(g9,g-10)
    c: Coincident(g10,g9)
    c: Coincident(g10,g-10)
    c: Coincident(g11,g10)
    c: Coincident(g11,g8)
    c: Coincident(g12,g-5)
    c: Coincident(g12,g-5)
    c: Coincident(g13,g12)
    c: Coincident(g13,g-9)
    c: Coincident(g14,g13)
    c: Coincident(g14,g-9)
    c: Coincident(g15,g14)
    c: Coincident(g15,g12)
FEATURE [PartDesign::Pad] Pad006
  BaseFeature = -> Mirrored005
  Direction = (0,-1,2e-16)
  Length = 0.63
  Length2 = 10
  Profile = -> Sketch012
  ReferenceAxis = -> Sketch012 [N_Axis]
  Refine = true
  Suppressed = false
  Type = 0
FEATURE [Sketcher::SketchObject] Sketch013
  ArcFitTolerance = 1e-06
  AttachmentSupport = -> [Pad006]
  ExternalGeometry = -> [Pad006]
  FullyConstrained = true
  MakeInternals = false
  MapMode = 5
  Placement = pos=(28.6,0,0) rot=(0.57735,-0.57735,-0.57735;2.0944rad)
  sketch-geometry (9):
    g0: LineSegment [constr] StartX=4.76 StartY=34.14 StartZ=0 EndX=4.76 EndY=19.14 EndZ=0
    g1: LineSegment StartX=2.76 StartY=34.14 StartZ=0 EndX=3.76 EndY=34.14 EndZ=0
    g2: LineSegment StartX=2.76 StartY=34.14 StartZ=0 EndX=2.76 EndY=19.14 EndZ=0
    g3: LineSegment StartX=3.76 StartY=34.14 StartZ=0 EndX=3.76 EndY=19.14 EndZ=0
    g4: LineSegment StartX=2.76 StartY=19.14 StartZ=0 EndX=3.76 EndY=19.14 EndZ=0
    g5: LineSegment StartX=6.76 StartY=34.14 StartZ=0 EndX=6.76 EndY=19.14 EndZ=0
    g6: LineSegment StartX=6.76 StartY=19.14 StartZ=0 EndX=5.76 EndY=19.14 EndZ=0
    g7: LineSegment StartX=5.76 StartY=34.14 StartZ=0 EndX=5.76 EndY=19.14 EndZ=0
    g8: LineSegment StartX=6.76 StartY=34.14 StartZ=0 EndX=5.76 EndY=34.14 EndZ=0
  constraints (27):
    c: Vertical(g0)
    c: PointOnObject(g0,g-3)
    c: Distance(g0,g-4) = 3.36
    c: Distance(g1) = 1
    c: Horizontal(g1)
    c: PointOnObject(g1,g-3)
    c: Vertical(g2)
    c: Coincident(g2,g1)
    c: Distance(g3) = 15
    c: Vertical(g3)
    c: Coincident(g3,g1)
    c: Coincident(g4,g2)
    c: Coincident(g4,g3)
    c: Equal(g0,g3)
    c: Equal(g3,g2)
    c: Distance(g0,g3) = 1
    c: Distance(g8) = 1
    c: Horizontal(g8)
    c: Vertical(g5)
    c: Coincident(g5,g8)
    c: Distance(g7) = 15
    c: Vertical(g7)
    c: Coincident(g7,g8)
    c: Coincident(g6,g5)
    c: Coincident(g6,g7)
    c: Equal(g7,g5)
    c: Symmetric(g6,g3,g0)
FEATURE [PartDesign::Pad] Pad007
  BaseFeature = -> Pad006
  Direction = (-1,0,0)
  Length = 2.66
  Length2 = 10
  Profile = -> Sketch013
  ReferenceAxis = -> Sketch013 [N_Axis]
  Refine = true
  Suppressed = false
  Type = 0
FEATURE [PartDesign::Plane] DatumPlane
  AttachmentOffset = pos=(0,0,53.5) rot=(0,0,1;0rad)
  AttachmentSupport = -> [Sketch013]
  Length = 91.037
  MapMode = 4
  Placement = pos=(28.6,-53.5,0) rot=(0.57735,-0.57735,0.57735;2.0944rad)
  ResizeMode = 0
  Width = 103.902
FEATURE [PartDesign::Mirrored] Mirrored006
  BaseFeature = -> Pad007
  MirrorPlane = -> DatumPlane
  Originals = -> [Pad007]
  Refine = true
  Suppressed = false
  TransformMode = 0
FEATURE [Sketcher::SketchObject] Sketch014
  ArcFitTolerance = 1e-06
  AttachmentSupport = -> [Mirrored006]
  ExternalGeometry = -> [Mirrored006]
  FullyConstrained = true
  MakeInternals = false
  MapMode = 5
  Placement = pos=(-28.6,0,0) rot=(0.57735,0.57735,0.57735;2.0944rad)
  sketch-geometry (16):
    g0: LineSegment StartX=-104.24 StartY=34.14 StartZ=0 EndX=-103.24 EndY=34.14 EndZ=0
    g1: LineSegment StartX=-104.24 StartY=34.14 StartZ=0 EndX=-104.24 EndY=19.14 EndZ=0
    g2: LineSegment StartX=-104.24 StartY=19.14 StartZ=0 EndX=-103.24 EndY=19.14 EndZ=0
    g3: LineSegment StartX=-103.24 StartY=19.14 StartZ=0 EndX=-103.24 EndY=34.14 EndZ=0
    g4: LineSegment StartX=-101.24 StartY=34.14 StartZ=0 EndX=-100.24 EndY=34.14 EndZ=0
    g5: LineSegment StartX=-101.24 StartY=34.14 StartZ=0 EndX=-101.24 EndY=19.14 EndZ=0
    g6: LineSegment StartX=-101.24 StartY=19.14 StartZ=0 EndX=-100.24 EndY=19.14 EndZ=0
    g7: LineSegment StartX=-100.24 StartY=19.14 StartZ=0 EndX=-100.24 EndY=34.14 EndZ=0
    g8: LineSegment StartX=-6.76 StartY=34.14 StartZ=0 EndX=-5.76 EndY=34.14 EndZ=0
    g9: LineSegment StartX=-6.76 StartY=34.14 StartZ=0 EndX=-6.76 EndY=19.14 EndZ=0
    g10: LineSegment StartX=-6.76 StartY=19.14 StartZ=0 EndX=-5.76 EndY=19.14 EndZ=0
    g11: LineSegment StartX=-5.76 StartY=19.14 StartZ=0 EndX=-5.76 EndY=34.14 EndZ=0
    g12: LineSegment StartX=-3.76 StartY=34.14 StartZ=0 EndX=-2.76 EndY=34.14 EndZ=0
    g13: LineSegment StartX=-3.76 StartY=34.14 StartZ=0 EndX=-3.76 EndY=19.14 EndZ=0
    g14: LineSegment StartX=-3.76 StartY=19.14 StartZ=0 EndX=-2.76 EndY=19.14 EndZ=0
    g15: LineSegment StartX=-2.76 StartY=19.14 StartZ=0 EndX=-2.76 EndY=34.14 EndZ=0
  constraints (32):
    c: Coincident(g0,g-6)
    c: Coincident(g0,g-6)
    c: Coincident(g1,g0)
    c: Coincident(g1,g-5)
    c: Coincident(g2,g1)
    c: Coincident(g2,g-4)
    c: Coincident(g3,g2)
    c: Coincident(g3,g0)
    c: Coincident(g4,g-9)
    c: Coincident(g4,g-8)
    c: Coincident(g5,g4)
    c: Coincident(g5,g-10)
    c: Coincident(g6,g5)
    c: Coincident(g6,g-10)
    c: Coincident(g7,g6)
    c: Coincident(g7,g4)
    c: Coincident(g8,g-14)
    c: Coincident(g8,g-14)
    c: Coincident(g9,g8)
    c: Coincident(g9,g-13)
    c: Coincident(g10,g9)
    c: Coincident(g10,g-12)
    c: Coincident(g11,g10)
    c: Coincident(g11,g8)
    c: Coincident(g12,g-17)
    c: Coincident(g12,g-16)
    c: Coincident(g13,g12)
    c: Coincident(g13,g-18)
    c: Coincident(g14,g13)
    c: Coincident(g14,g-18)
    c: Coincident(g15,g14)
    c: Coincident(g15,g12)
FEATURE [PartDesign::Pad] Pad008
  BaseFeature = -> Mirrored006
  Direction = (1,0,0)
  Length = 2.66
  Length2 = 10
  Profile = -> Sketch014
  ReferenceAxis = -> Sketch014 [N_Axis]
  Refine = true
  Suppressed = false
  Type = 0
FEATURE [PartDesign::Fillet] Fillet003
  Base = -> Pad008 [Edge379,Edge371,Edge373]
  BaseFeature = -> Pad008
  Radius = 2
  Refine = true
  SupportTransform = false
  Suppressed = false
  UseAllEdges = false
FEATURE [PartDesign::Body] Body001
  AllowCompound = false
  Group = -> [Sketch,Pad,Thickness,Thickness001,Sketch001,Pocket,Sketch002,Pad001,Sketch003,Pad002,Sketch004,Pad003,Sketch005,Pad004,Mirrored,Sketch006,Pocket001,Mirrored001,Sketch007,Pocket002,Mirrored002,Fillet,Mirrored003,Sketch008,Pocket003,Sketch009,Pocket004,Mirrored004,Fillet001,Sketch010,Pocket005,Fillet002,Sketch011,Pad005,Mirrored005,Sketch012,Pad006,Sketch013,Pad007,DatumPlane,Mirrored006,Sketch014,+2 more]
  Origin = -> Origin001
  Tip = -> Fillet003
